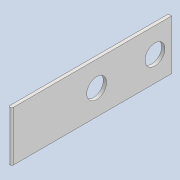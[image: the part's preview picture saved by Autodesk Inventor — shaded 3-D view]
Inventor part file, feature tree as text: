
AUTODESK INVENTOR PART (.ipt)
format: ipt  version: 2020 (Build 240168000, 168)  size: 114,688 bytes
history: native  units: mm
features: extrude x4, sketch x4, projected_geometry x1
ambient origin geometry x8: Origin, YZ Plane, XZ Plane, XY Plane, X Axis, Y Axis, Z Axis, Center Point
bodies: Solid1 (feature_tree)
feature tree (9):
  extrude  "Extrusion1"  Depth=0.2mm
  extrude  "Extrusion2"  Depth=3.0mm
  extrude  "Extrusion3"  Depth=3.0mm TaperAngle=0.0deg
  extrude  "Extrusion4"  Depth=10.0mm
  sketch  "Sketch1"  dims[d0=12.0mm d1=0.2mm]
  sketch  "Sketch2"  dims[d2=3.0mm d3=0.0mm d4=2.0mm]
  sketch  "Sketch3"  dims[d5=1.2mm d6=3.0mm d7=0.0mm]
  sketch  "Sketch4"  dims[d8=5.0mm d9=3.5mm d10=1.2mm d11=1.2mm d12=10.0mm d13=0.0mm d14=2.5mm d15=0.8mm d16=3.0mm d17=10.0mm d18=0.0mm]
  projected_geometry  "Projected Loop1"
